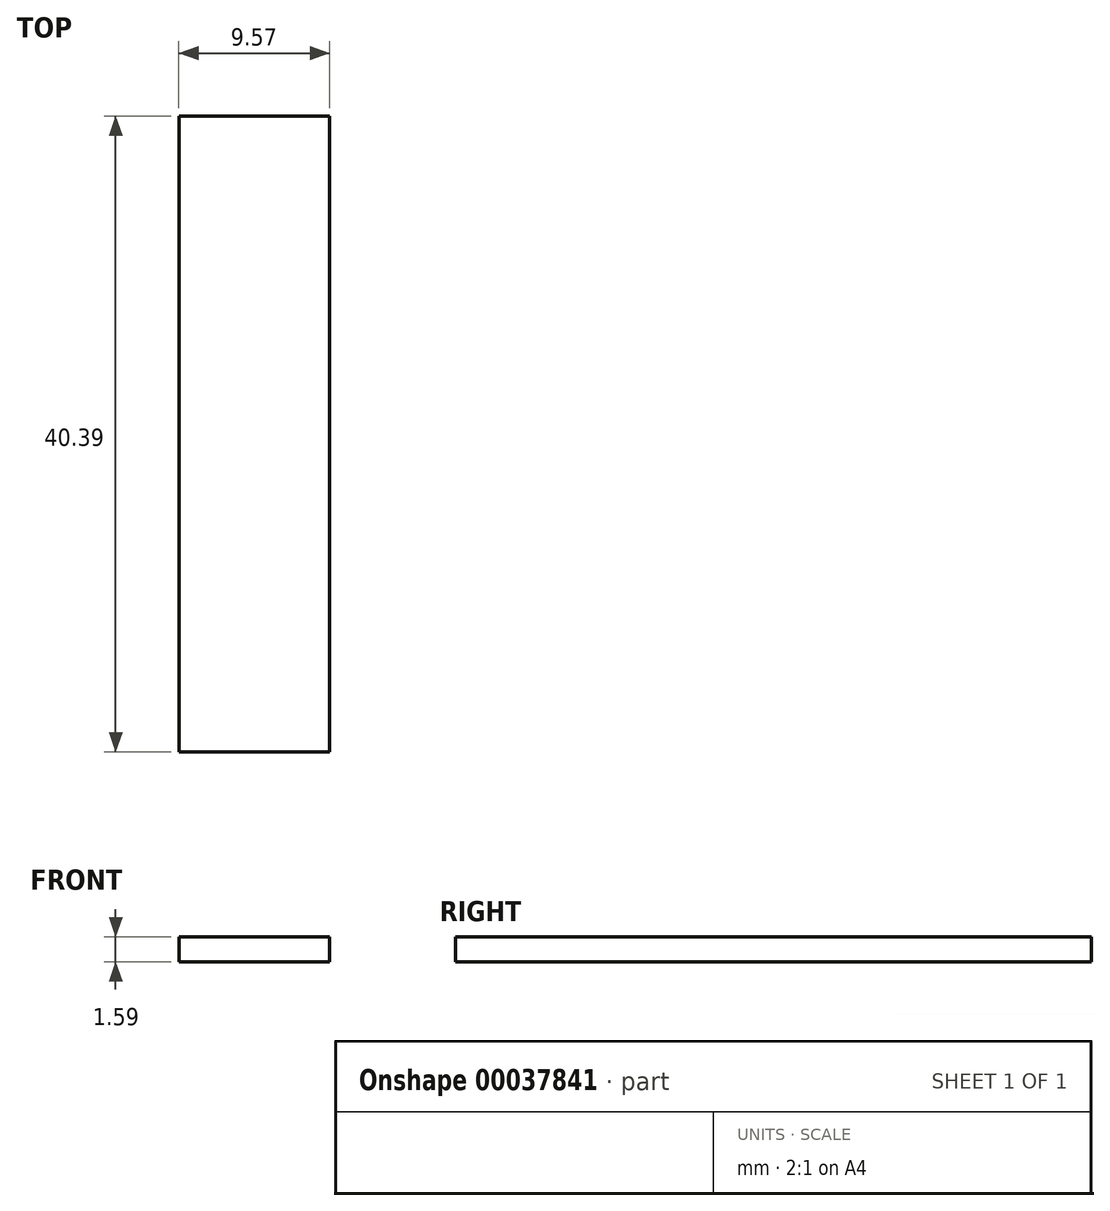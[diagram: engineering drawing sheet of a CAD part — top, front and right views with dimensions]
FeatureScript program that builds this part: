
annotation { "Feature Type Name" : "Feature", "Feature Type Description" : "" }
export const myFeature = defineFeature(function(context is Context, id is Id, definition is map)
    precondition{}
    {
        {
            var Q0;
            Q0=qCreatedBy(makeId("Top.planeOp"),FACE);
            var sketch = newSketch(context, id + "F0", { "sketchPlane" : qUnion([Q0])});
            skLineSegment(sketch, "E0.bottom", {"start": v(0, 0) * mm, "end": v(-9.57, 0) * mm});
            skLineSegment(sketch, "E0.top", {"start": v(0, -40.39) * mm, "end": v(-9.57, -40.39) * mm});
            skLineSegment(sketch, "E0.left", {"start": v(0, 0) * mm, "end": v(0, -40.39) * mm});
            skLineSegment(sketch, "E0.right", {"start": v(-9.57, 0) * mm, "end": v(-9.57, -40.39) * mm});
            skSolve(sketch);
        }
        {
            var Q0;
            Q0 = qSketchRegion(id + "F0", true);
            extrude(context, id + "F1", {"entities" : qUnion([Q0]), "depth" : 1.59 * mm});
        }
    });
